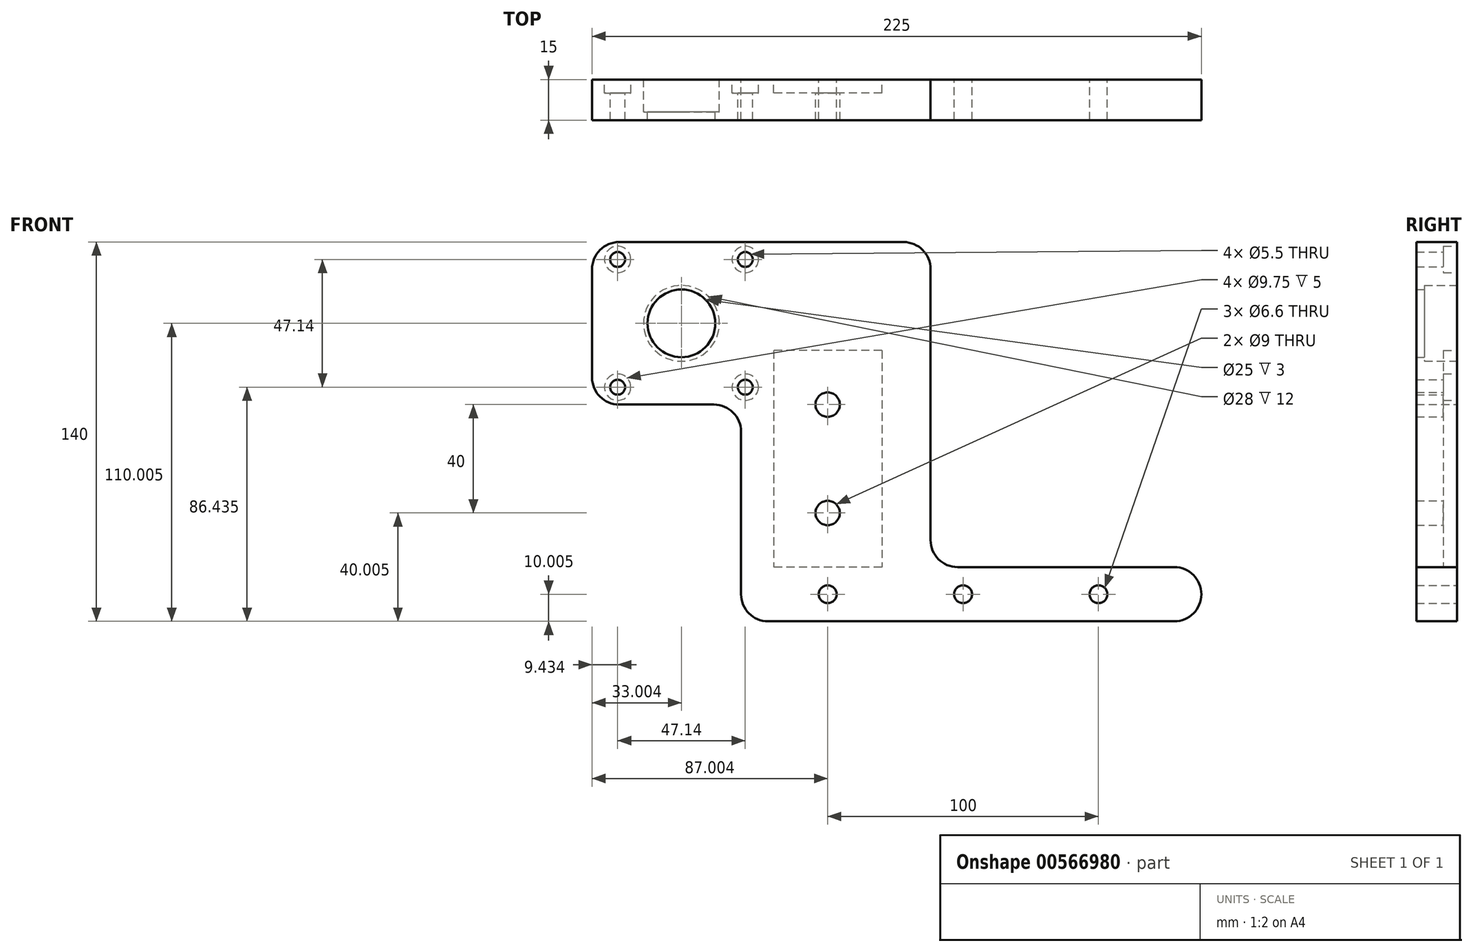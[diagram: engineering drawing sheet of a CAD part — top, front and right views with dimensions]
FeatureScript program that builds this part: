
annotation { "Feature Type Name" : "Feature", "Feature Type Description" : "" }
export const myFeature = defineFeature(function(context is Context, id is Id, definition is map)
    precondition{}
    {
        {
            var Q0;
            Q0=qCreatedBy(makeId("Front.planeOp"),FACE);
            var sketch = newSketch(context, id + "F0", { "sketchPlane" : qUnion([Q0])});
            skLineSegment(sketch, "E0", {"start": v(-57.93, 20.91) * mm, "end": v(62.07, 20.91) * mm});
            skLineSegment(sketch, "E1", {"start": v(62.07, 20.91) * mm, "end": v(62.07, -99.09) * mm});
            skLineSegment(sketch, "E2", {"start": v(62.07, -99.09) * mm, "end": v(162.07, -99.09) * mm});
            skLineSegment(sketch, "E3", {"start": v(162.07, -99.09) * mm, "end": v(162.07, -119.09) * mm});
            skLineSegment(sketch, "E4", {"start": v(162.07, -119.09) * mm, "end": v(-7.93, -119.09) * mm});
            skLineSegment(sketch, "E5", {"start": v(-7.93, -119.09) * mm, "end": v(-7.93, -39.09) * mm});
            skLineSegment(sketch, "E6", {"start": v(-7.93, -39.09) * mm, "end": v(-57.93, -39.09) * mm});
            skLineSegment(sketch, "E7", {"start": v(52.07, 10.91) * mm, "end": v(-47.93, 10.91) * mm, "construction": true});
            skLineSegment(sketch, "E8", {"start": v(-47.93, 10.91) * mm, "end": v(-47.93, -29.09) * mm, "construction": true});
            skLineSegment(sketch, "E9", {"start": v(-47.93, -29.09) * mm, "end": v(4.07, -29.09) * mm, "construction": true});
            skLineSegment(sketch, "E10", {"start": v(4.07, -29.09) * mm, "end": v(4.07, -119.09) * mm, "construction": true});
            skLineSegment(sketch, "E11", {"start": v(4.07, -119.09) * mm, "end": v(162.07, -119.09) * mm, "construction": true});
            skLineSegment(sketch, "E12", {"start": v(162.07, -119.09) * mm, "end": v(162.07, -99.09) * mm, "construction": true});
            skLineSegment(sketch, "E13", {"start": v(162.07, -99.09) * mm, "end": v(52.07, -99.09) * mm, "construction": true});
            skLineSegment(sketch, "E14", {"start": v(52.07, -99.09) * mm, "end": v(52.07, 10.91) * mm, "construction": true});
            skPoint(sketch, "E15", {"position": v(24.07, -109.09) * mm});
            skPoint(sketch, "E16", {"position": v(24.07, -79.09) * mm});
            skPoint(sketch, "E17", {"position": v(24.07, -39.09) * mm});
            skPoint(sketch, "E18", {"position": v(74.07, -109.09) * mm});
            skPoint(sketch, "E19", {"position": v(124.07, -109.09) * mm});
            skPoint(sketch, "E20", {"position": v(-29.93, -9.09) * mm});
            skPoint(sketch, "E21", {"position": v(-53.5, 14.48) * mm});
            skLineSegment(sketch, "E22", {"start": v(-44.33, -9.09) * mm, "end": v(-15.97, -9.09) * mm, "construction": true});
            skLineSegment(sketch, "E23", {"start": v(-29.93, 7.3) * mm, "end": v(-29.93, -21.44) * mm, "construction": true});
            skPoint(sketch, "E24.MirrorP", {"position": v(-53.5, -32.66) * mm});
            skPoint(sketch, "E25.MirrorP", {"position": v(-6.36, 14.48) * mm});
            skPoint(sketch, "E26.MirrorP", {"position": v(-6.36, -32.66) * mm});
            skLineSegment(sketch, "E27", {"start": v(-57.93, 20.91) * mm, "end": v(-62.93, 20.91) * mm});
            skLineSegment(sketch, "E28", {"start": v(-62.93, 20.91) * mm, "end": v(-62.93, -39.09) * mm});
            skLineSegment(sketch, "E29", {"start": v(-62.93, -39.09) * mm, "end": v(-57.93, -39.09) * mm});
            skSolve(sketch);
        }
        {
            var Q0;
            Q0=makeQuery(id+"F0.imprint","IMPRINT",FACE,{"disambiguationData":[TD([[makeQuery(id+"F0.imprint","IMPRINT",EDGE,{"derivedFrom":sQuery(id+"F0.wireOp",EDGE,"E0")}),-1.0]])]});
            extrude(context, id + "F1", {"entities" : qUnion([Q0]), "depth" : 15 * mm});
        }
        {
            var Q0;
            Q0=sQuery(id+"F0.wireOp",VERTEX,"E16");
            var Q1;
            Q1=sQuery(id+"F0.wireOp",VERTEX,"E17");
            var Q2;
            Q2=makeQuery(id+"F1.opExtrude","SWEPT_BODY",BODY,{"disambiguationData":[OSD([sQuery(id+"F0.wireOp",EDGE,"E0"),sQuery(id+"F0.wireOp",EDGE,"E1"),sQuery(id+"F0.wireOp",EDGE,"E2"),sQuery(id+"F0.wireOp",EDGE,"E3"),sQuery(id+"F0.wireOp",EDGE,"E4"),sQuery(id+"F0.wireOp",EDGE,"E5"),sQuery(id+"F0.wireOp",EDGE,"E6"),sQuery(id+"F0.wireOp",EDGE,"cvZF5QLb-uWAo-robz-iAHo-1Gj3ORty2Von")])]});
            hole(context, id + "F2", {"style" : HoleStyle.SIMPLE, "endStyle" : HoleEndStyle.THROUGH, "oppositeDirection" : true, "holeDiameter" : 9 * mm, "locations" : qUnion([Q0, Q1]), "scope" : qUnion([Q2]), "tappedDepth" : 12 * mm, "tapClearance" : 3});
        }
        {
            var Q0;
            Q0=sQuery(id+"F0.wireOp",VERTEX,"E15");
            var Q1;
            Q1=sQuery(id+"F0.wireOp",VERTEX,"E18");
            var Q2;
            Q2=sQuery(id+"F0.wireOp",VERTEX,"E19");
            var Q3;
            Q3=makeQuery(id+"F1.opExtrude","SWEPT_BODY",BODY,{"disambiguationData":[OSD([sQuery(id+"F0.wireOp",EDGE,"E0"),sQuery(id+"F0.wireOp",EDGE,"E1"),sQuery(id+"F0.wireOp",EDGE,"E2"),sQuery(id+"F0.wireOp",EDGE,"E3"),sQuery(id+"F0.wireOp",EDGE,"E4"),sQuery(id+"F0.wireOp",EDGE,"E5"),sQuery(id+"F0.wireOp",EDGE,"E6"),sQuery(id+"F0.wireOp",EDGE,"cvZF5QLb-uWAo-robz-iAHo-1Gj3ORty2Von")])]});
            hole(context, id + "F3", {"style" : HoleStyle.SIMPLE, "endStyle" : HoleEndStyle.THROUGH, "oppositeDirection" : true, "standardTappedOrClearance" : lookupTablePath({ "standard" : "ISO", "fit" : "Normal", "size" : "M6", "type" : "Clearance" }), "standardBlindInLast" : lookupTablePath({ "fit" : "Standard", "standard" : "ISO", "size" : "M6", "type" : "Clearance" }), "holeDiameter" : 6.6 * mm, "locations" : qUnion([Q0, Q1, Q2]), "scope" : qUnion([Q3]), "isTappedThrough" : true});
        }
        {
            var Q0;
            Q0=makeQuery(id+"F1.opExtrude","SWEPT_EDGE",EDGE,{"disambiguationData":[OSD([sQuery(id+"F0.wireOp",EDGE,"E0"),sQuery(id+"F0.wireOp",EDGE,"cvZF5QLb-uWAo-robz-iAHo-1Gj3ORty2Von")])]});
            var Q1;
            Q1=makeQuery(id+"F1.opExtrude","SWEPT_EDGE",EDGE,{"disambiguationData":[OSD([sQuery(id+"F0.wireOp",EDGE,"E1"),sQuery(id+"F0.wireOp",EDGE,"E2")])]});
            var Q2;
            Q2=makeQuery(id+"F1.opExtrude","SWEPT_EDGE",EDGE,{"disambiguationData":[OSD([sQuery(id+"F0.wireOp",EDGE,"E0"),sQuery(id+"F0.wireOp",EDGE,"E1")])]});
            var Q3;
            Q3=makeQuery(id+"F1.opExtrude","SWEPT_EDGE",EDGE,{"disambiguationData":[OSD([sQuery(id+"F0.wireOp",EDGE,"E3"),sQuery(id+"F0.wireOp",EDGE,"E4")])]});
            var Q4;
            Q4=makeQuery(id+"F1.opExtrude","SWEPT_EDGE",EDGE,{"disambiguationData":[OSD([sQuery(id+"F0.wireOp",EDGE,"E2"),sQuery(id+"F0.wireOp",EDGE,"E3")])]});
            var Q5;
            Q5=makeQuery(id+"F1.opExtrude","SWEPT_EDGE",EDGE,{"disambiguationData":[OSD([sQuery(id+"F0.wireOp",EDGE,"E4"),sQuery(id+"F0.wireOp",EDGE,"E5")])]});
            var Q6;
            Q6=makeQuery(id+"F1.opExtrude","SWEPT_EDGE",EDGE,{"disambiguationData":[OSD([sQuery(id+"F0.wireOp",EDGE,"E5"),sQuery(id+"F0.wireOp",EDGE,"E6")])]});
            var Q7;
            Q7=makeQuery(id+"F1.opExtrude","SWEPT_EDGE",EDGE,{"disambiguationData":[OSD([sQuery(id+"F0.wireOp",EDGE,"E6"),sQuery(id+"F0.wireOp",EDGE,"cvZF5QLb-uWAo-robz-iAHo-1Gj3ORty2Von")])]});
            var Q8;
            Q8=makeQuery(id+"F1.opExtrude","SWEPT_EDGE",EDGE,{"disambiguationData":[OSD([sQuery(id+"F0.wireOp",EDGE,"E27"),sQuery(id+"F0.wireOp",EDGE,"E28")])]});
            var Q9;
            Q9=makeQuery(id+"F1.opExtrude","SWEPT_EDGE",EDGE,{"disambiguationData":[OSD([sQuery(id+"F0.wireOp",EDGE,"E28"),sQuery(id+"F0.wireOp",EDGE,"E29")])]});
            fillet(context, id + "F4", {"entities" : qUnion([Q0, Q1, Q2, Q3, Q4, Q5, Q6, Q7, Q8, Q9]), "radius" : 10 * mm, "tangentPropagation" : true, "allowEdgeOverflow" : false});
        }
        {
            var Q0;
            Q0=sQuery(id+"F0.wireOp",VERTEX,"E20");
            var Q1;
            Q1=makeQuery(id+"F1.opExtrude","SWEPT_BODY",BODY,{"disambiguationData":[OSD([sQuery(id+"F0.wireOp",EDGE,"E0"),sQuery(id+"F0.wireOp",EDGE,"E1"),sQuery(id+"F0.wireOp",EDGE,"E2"),sQuery(id+"F0.wireOp",EDGE,"E3"),sQuery(id+"F0.wireOp",EDGE,"E4"),sQuery(id+"F0.wireOp",EDGE,"E5"),sQuery(id+"F0.wireOp",EDGE,"E6"),sQuery(id+"F0.wireOp",EDGE,"cvZF5QLb-uWAo-robz-iAHo-1Gj3ORty2Von")])]});
            hole(context, id + "F5", {"style" : HoleStyle.C_BORE, "endStyle" : HoleEndStyle.THROUGH, "oppositeDirection" : true, "holeDiameter" : 25 * mm, "cBoreDiameter" : 28 * mm, "cBoreDepth" : 12 * mm, "locations" : qUnion([Q0]), "scope" : qUnion([Q1]), "tappedDepth" : 12 * mm, "tapClearance" : 3});
        }
        {
            var Q0;
            Q0=sQuery(id+"F0.wireOp",VERTEX,"E21");
            var Q1;
            Q1=sQuery(id+"F0.wireOp",VERTEX,"E25.MirrorP");
            var Q2;
            Q2=sQuery(id+"F0.wireOp",VERTEX,"E26.MirrorP");
            var Q3;
            Q3=sQuery(id+"F0.wireOp",VERTEX,"E24.MirrorP");
            var Q4;
            Q4=makeQuery(id+"F1.opExtrude","SWEPT_BODY",BODY,{"disambiguationData":[OSD([sQuery(id+"F0.wireOp",EDGE,"E0"),sQuery(id+"F0.wireOp",EDGE,"E1"),sQuery(id+"F0.wireOp",EDGE,"E2"),sQuery(id+"F0.wireOp",EDGE,"E3"),sQuery(id+"F0.wireOp",EDGE,"E4"),sQuery(id+"F0.wireOp",EDGE,"E5"),sQuery(id+"F0.wireOp",EDGE,"E6"),sQuery(id+"F0.wireOp",EDGE,"cvZF5QLb-uWAo-robz-iAHo-1Gj3ORty2Von")])]});
            hole(context, id + "F6", {"style" : HoleStyle.C_BORE, "endStyle" : HoleEndStyle.THROUGH, "oppositeDirection" : true, "standardTappedOrClearance" : lookupTablePath({ "standard" : "ISO", "fit" : "Normal", "size" : "M5", "type" : "Clearance" }), "standardBlindInLast" : lookupTablePath({ "fit" : "Standard", "standard" : "ISO", "size" : "M5", "type" : "Clearance" }), "holeDiameter" : 5.5 * mm, "cBoreDiameter" : 9.75 * mm, "cBoreDepth" : 5 * mm, "locations" : qUnion([Q0, Q1, Q2, Q3]), "scope" : qUnion([Q4]), "tappedDepth" : 12 * mm, "tapClearance" : 3});
        }
        {
            var Q0;
            Q0=makeQuery(id+"F0.imprint","IMPRINT",FACE,{"disambiguationData":[TD([[makeQuery(id+"F0.imprint","IMPRINT",EDGE,{"derivedFrom":sQuery(id+"F0.wireOp",EDGE,"E0")}),-1.0]])]});
            var sketch = newSketch(context, id + "F7", { "sketchPlane" : qUnion([Q0])});
            skLineSegment(sketch, "E30.bottom", {"start": v(44.07, -19.09) * mm, "end": v(4.07, -19.09) * mm});
            skLineSegment(sketch, "E30.top", {"start": v(44.07, -99.09) * mm, "end": v(4.07, -99.09) * mm});
            skLineSegment(sketch, "E30.left", {"start": v(44.07, -19.09) * mm, "end": v(44.07, -99.09) * mm});
            skLineSegment(sketch, "E30.right", {"start": v(4.07, -19.09) * mm, "end": v(4.07, -99.09) * mm});
            skSolve(sketch);
        }
        {
            var Q0;
            Q0=qSketchRegion(id+"F7",true);
            extrude(context, id + "F8", {"entities" : qUnion([Q0]), "operationType" : NewBodyOperationType.REMOVE, "depth" : 5 * mm});
        }
    });
